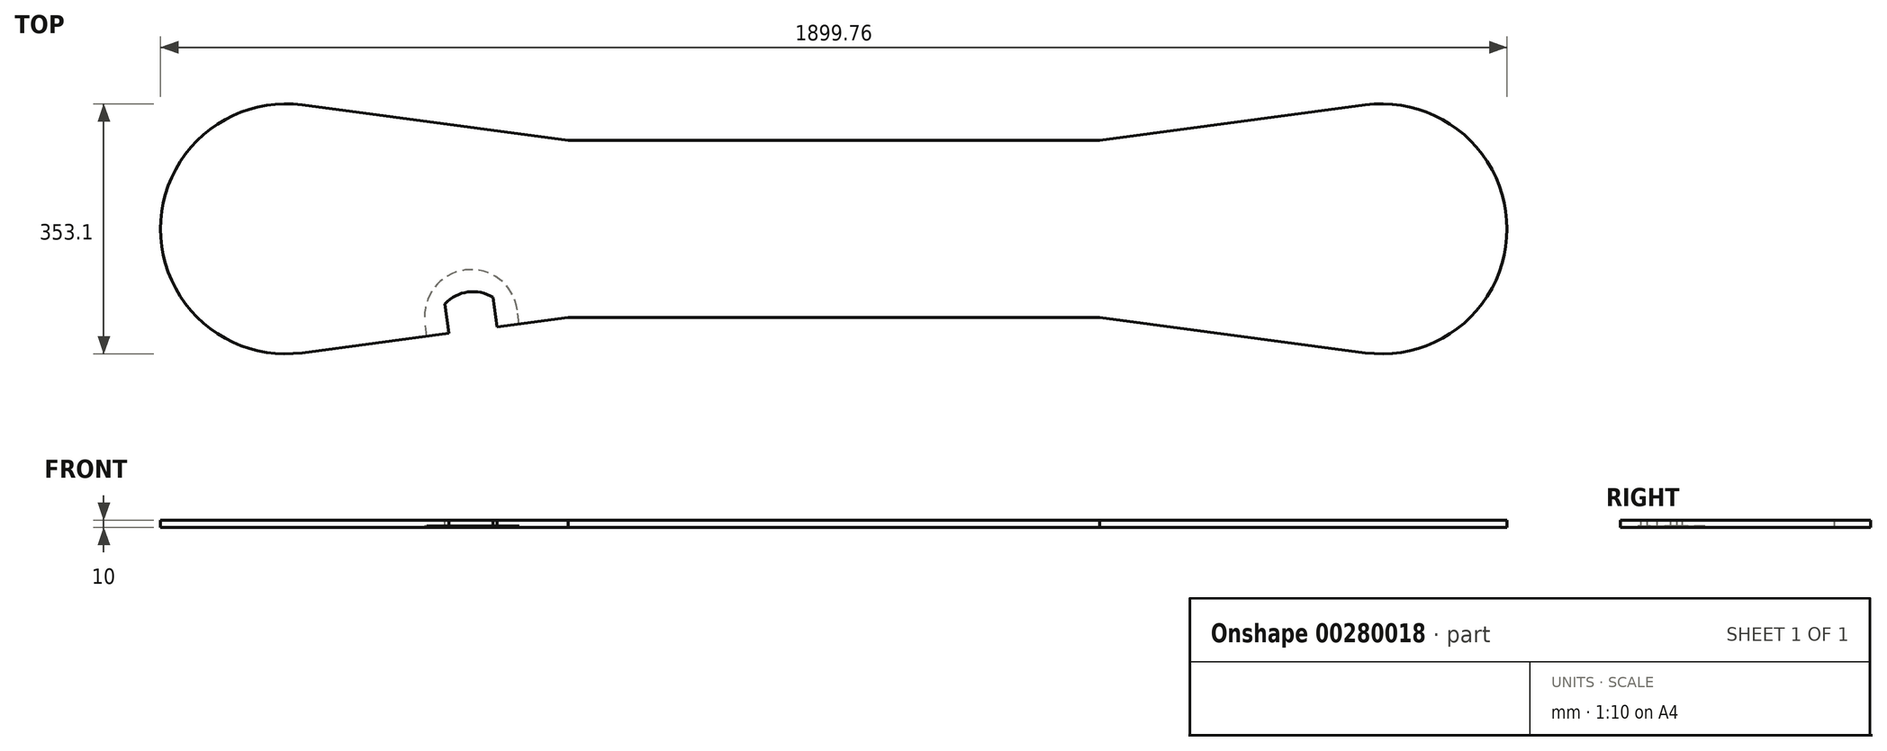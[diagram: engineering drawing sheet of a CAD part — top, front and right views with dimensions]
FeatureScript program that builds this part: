
annotation { "Feature Type Name" : "Feature", "Feature Type Description" : "" }
export const myFeature = defineFeature(function(context is Context, id is Id, definition is map)
    precondition{}
    {
        {
            assignVariable(context, id + "F0", {"name" : "Epaisseur_board_mm", "anyValue" : 10});
        }
        {
            var Q0;
            Q0=qCreatedBy(makeId("Top.planeOp"),FACE);
            var sketch = newSketch(context, id + "F1", { "sketchPlane" : qUnion([Q0])});
            skLineSegment(sketch, "E0", {"start": v(0, 125) * mm, "end": v(375, 125) * mm});
            skLineSegment(sketch, "E1", {"start": v(375, 125) * mm, "end": v(750, 175) * mm});
            skLineSegment(sketch, "E2.MirrorCS", {"start": v(0, -125) * mm, "end": v(375, -125) * mm});
            skLineSegment(sketch, "E3.MirrorCS", {"start": v(375, -125) * mm, "end": v(750, -175) * mm});
            skArc(sketch, "E4", {"start": v(750, 175) * mm, "mid": v(949.88, 0) * mm, "end": v(750, -175) * mm});
            skLineSegment(sketch, "E5.MirrorCS", {"start": v(0, 125) * mm, "end": v(-375, 125) * mm});
            skLineSegment(sketch, "E6.MirrorCS", {"start": v(-375, 125) * mm, "end": v(-750, 175) * mm});
            skArc(sketch, "E7.MirrorCS", {"start": v(-750, 175) * mm, "mid": v(-949.88, 0) * mm, "end": v(-750, -175) * mm});
            skLineSegment(sketch, "E8.MirrorCS", {"start": v(-375, -125) * mm, "end": v(-750, -175) * mm});
            skLineSegment(sketch, "E9.MirrorCS", {"start": v(0, -125) * mm, "end": v(-375, -125) * mm});
            skLineSegment(sketch, "E10", {"start": v(-105.83, 0) * mm, "end": v(109.17, 0) * mm, "construction": true});
            skSolve(sketch);
        }
        {
            var Q0;
            Q0=makeQuery(id+"F1.imprint","IMPRINT",FACE,{"disambiguationData":[TD([[makeQuery(id+"F1.imprint","IMPRINT",EDGE,{"derivedFrom":sQuery(id+"F1.wireOp",EDGE,"E0")}),-1.0]])]});
            extrude(context, id + "F2", {"entities" : qUnion([Q0]), "depth" : (getVariable(context, 'Epaisseur_board_mm')) * mm});
        }
        {
            var Q0;
            Q0=makeQuery(id+"F2.opExtrude","CAP_FACE",FACE,{"disambiguationData":[OSD([sQuery(id+"F1.wireOp",EDGE,"E0"),sQuery(id+"F1.wireOp",EDGE,"E1"),sQuery(id+"F1.wireOp",EDGE,"E2.MirrorCS"),sQuery(id+"F1.wireOp",EDGE,"E3.MirrorCS"),sQuery(id+"F1.wireOp",EDGE,"E4"),sQuery(id+"F1.wireOp",EDGE,"E5.MirrorCS"),sQuery(id+"F1.wireOp",EDGE,"E6.MirrorCS"),sQuery(id+"F1.wireOp",EDGE,"E7.MirrorCS"),sQuery(id+"F1.wireOp",EDGE,"E8.MirrorCS"),sQuery(id+"F1.wireOp",EDGE,"E9.MirrorCS")])],"isStart":false});
            var sketch = newSketch(context, id + "F3", { "sketchPlane" : qUnion([Q0])});
            skLineSegment(sketch, "E11", {"start": v(-475, -138.33) * mm, "end": v(-480.55, -96.7) * mm});
            skLineSegment(sketch, "E12", {"start": v(-543, -147.4) * mm, "end": v(-548.55, -105.77) * mm});
            skArc(sketch, "E13", {"start": v(-480.55, -96.7) * mm, "mid": v(-516.17, -89.12) * mm, "end": v(-548.55, -105.77) * mm});
            skLineSegment(sketch, "E14", {"start": v(-506.53, -161.41) * mm, "end": v(-531.6, 26.58) * mm, "construction": true});
            skSolve(sketch);
        }
        {
            var Q0;
            {var subQ0=sQuery(id+"F3.wireOp",EDGE,"E11");Q0=makeQuery(id+"F3.imprint","IMPRINT",FACE,{"disambiguationData":[TD([[makeQuery(id+"F3.imprint","IMPRINT",EDGE,{"derivedFrom":subQ0}),1.0]])]});}
            extrude(context, id + "F4", {"entities" : qUnion([Q0]), "operationType" : NewBodyOperationType.REMOVE, "endBound" : BoundingType.THROUGH_ALL, "oppositeDirection" : true, "depth" : 25 * mm});
        }
        {
            var Q0;
            Q0=makeQuery(id+"F2.opExtrude","CAP_FACE",FACE,{"disambiguationData":[OSD([sQuery(id+"F1.wireOp",EDGE,"E0"),sQuery(id+"F1.wireOp",EDGE,"E1"),sQuery(id+"F1.wireOp",EDGE,"E2.MirrorCS"),sQuery(id+"F1.wireOp",EDGE,"E3.MirrorCS"),sQuery(id+"F1.wireOp",EDGE,"E4"),sQuery(id+"F1.wireOp",EDGE,"E5.MirrorCS"),sQuery(id+"F1.wireOp",EDGE,"E6.MirrorCS"),sQuery(id+"F1.wireOp",EDGE,"E7.MirrorCS"),sQuery(id+"F1.wireOp",EDGE,"E8.MirrorCS"),sQuery(id+"F1.wireOp",EDGE,"E9.MirrorCS")])],"isStart":true});
            var sketch = newSketch(context, id + "F5", { "sketchPlane" : qUnion([Q0])});
            skLineSegment(sketch, "E15", {"start": v(-574, 151.53) * mm, "end": v(-576.64, 131.7) * mm});
            skLineSegment(sketch, "E16", {"start": v(-444, 134.2) * mm, "end": v(-446.64, 114.38) * mm});
            skArc(sketch, "E17", {"start": v(-576.64, 131.7) * mm, "mid": v(-520.3, 58.04) * mm, "end": v(-446.64, 114.38) * mm});
            skSolve(sketch);
        }
        {
            var Q0;
            {var subQ8=sQuery(id+"F5.wireOp",EDGE,"E15");Q0=makeQuery(id+"F5.imprint","IMPRINT",FACE,{"disambiguationData":[TD([[makeQuery(id+"F5.imprint","IMPRINT",EDGE,{"derivedFrom":subQ8}),1.0]])]});}
            extrude(context, id + "F6", {"entities" : qUnion([Q0]), "operationType" : NewBodyOperationType.REMOVE, "oppositeDirection" : true, "depth" : 2 * mm});
        }
    });
